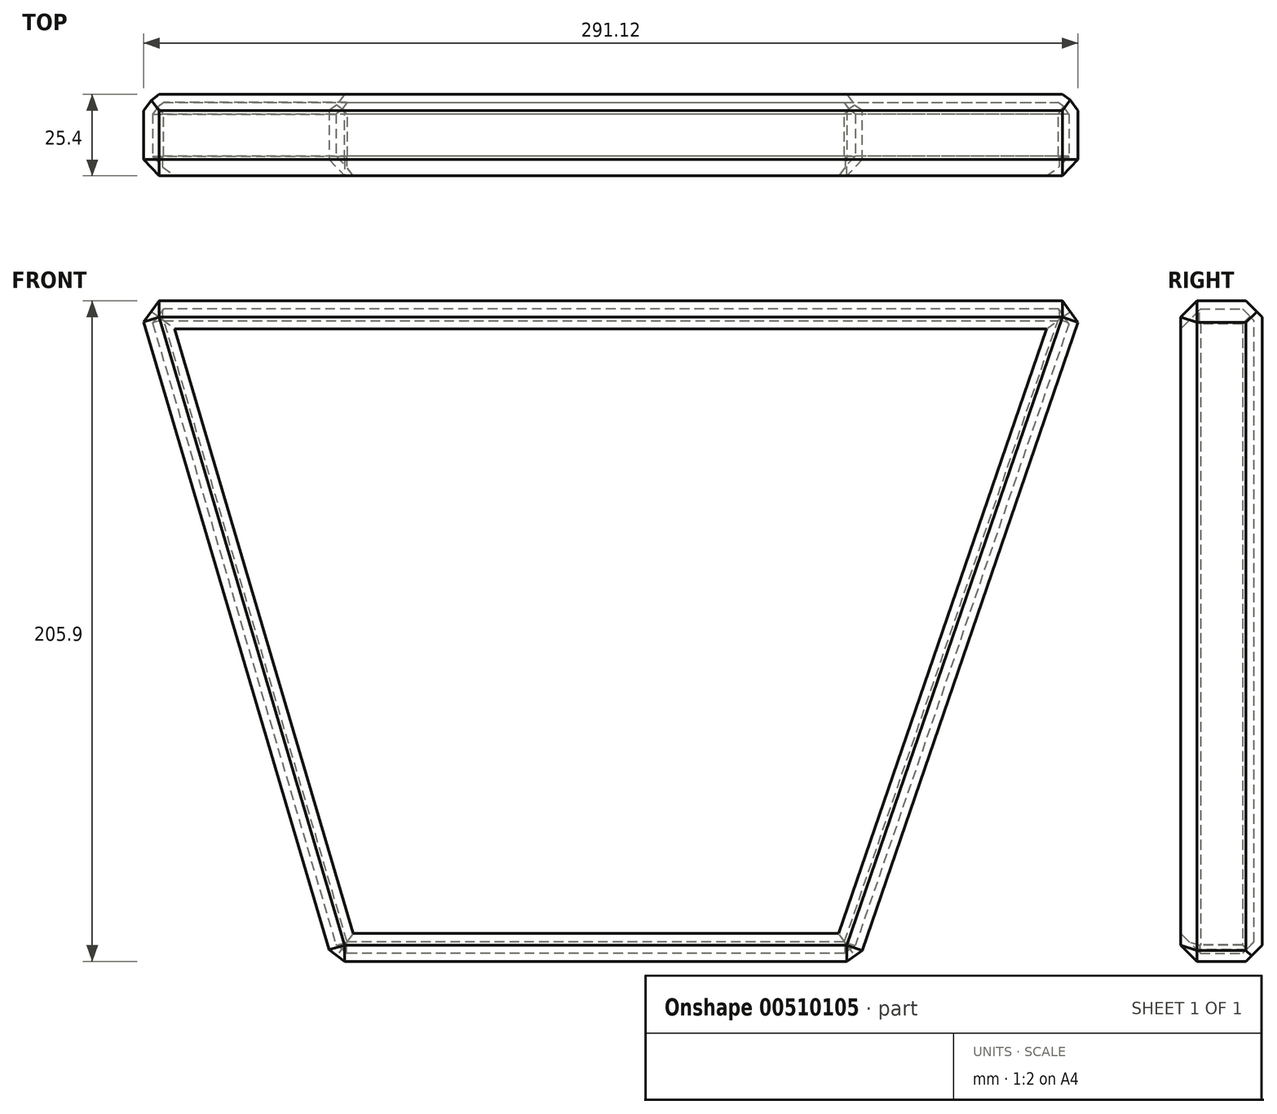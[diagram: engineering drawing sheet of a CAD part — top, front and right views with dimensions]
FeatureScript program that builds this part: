
annotation { "Feature Type Name" : "Feature", "Feature Type Description" : "" }
export const myFeature = defineFeature(function(context is Context, id is Id, definition is map)
    precondition{}
    {
        {
            var Q0;
            Q0=qCreatedBy(makeId("Front.planeOp"),FACE);
            var sketch = newSketch(context, id + "F0", { "sketchPlane" : qUnion([Q0])});
            skLineSegment(sketch, "E0.bottom", {"start": v(-83.09, -100.97) * mm, "end": v(80.84, -100.97) * mm});
            skLineSegment(sketch, "E0.top", {"start": v(-83.09, 104.93) * mm, "end": v(80.84, 104.93) * mm});
            skLineSegment(sketch, "E0.left", {"start": v(-83.09, -100.97) * mm, "end": v(-83.09, 104.93) * mm});
            skLineSegment(sketch, "E0.right", {"start": v(80.84, -100.97) * mm, "end": v(80.84, 104.93) * mm});
            skPoint(sketch, "E0.middle", {"position": v(-1.12, 1.98) * mm});
            skLineSegment(sketch, "E1", {"start": v(-83.09, -100.97) * mm, "end": v(-143.8, 104.93) * mm});
            skLineSegment(sketch, "E2", {"start": v(-143.8, 104.93) * mm, "end": v(-83.09, 104.93) * mm});
            skLineSegment(sketch, "E3", {"start": v(80.84, -100.97) * mm, "end": v(151.55, 104.93) * mm});
            skLineSegment(sketch, "E4", {"start": v(151.55, 104.93) * mm, "end": v(80.84, 104.93) * mm});
            skSolve(sketch);
        }
        {
            var Q0;
            Q0=makeQuery(id+"F0.imprint","IMPRINT",FACE,{"disambiguationData":[TD([[makeQuery(id+"F0.imprint","IMPRINT",EDGE,{"derivedFrom":sQuery(id+"F0.wireOp",EDGE,"E0.left")}),1.0]])]});
            var Q1;
            Q1=makeQuery(id+"F0.imprint","IMPRINT",FACE,{"disambiguationData":[TD([[makeQuery(id+"F0.imprint","IMPRINT",EDGE,{"derivedFrom":sQuery(id+"F0.wireOp",EDGE,"E0.right")}),-1.0]])]});
            var Q2;
            Q2=makeQuery(id+"F0.imprint","IMPRINT",FACE,{"disambiguationData":[TD([[makeQuery(id+"F0.imprint","IMPRINT",EDGE,{"derivedFrom":sQuery(id+"F0.wireOp",EDGE,"E0.bottom")}),1.0]])]});
            extrude(context, id + "F1", {"entities" : qUnion([Q0, Q1, Q2]), "depth" : 25.4 * mm});
        }
        {
            var Q0;
            Q0=makeQuery(id+"F1.opExtrude","CAP_FACE",FACE,{"disambiguationData":[OSD([sQuery(id+"F0.wireOp",EDGE,"E0.bottom"),sQuery(id+"F0.wireOp",EDGE,"E0.top"),sQuery(id+"F0.wireOp",EDGE,"E1"),sQuery(id+"F0.wireOp",EDGE,"E2"),sQuery(id+"F0.wireOp",EDGE,"E3"),sQuery(id+"F0.wireOp",EDGE,"E4")])],"isStart":true});
            chamfer(context, id + "F2", {"entities" : qUnion([Q0]), "width" : 5.08 * mm, "tangentPropagation" : true});
        }
        {
            var Q0;
            Q0=makeQuery(id+"F1.opExtrude","CAP_EDGE",EDGE,{"disambiguationData":[OSD([sQuery(id+"F0.wireOp",EDGE,"E0.bottom")])],"isStart":false});
            var Q1;
            Q1=makeQuery(id+"F1.opExtrude","CAP_EDGE",EDGE,{"disambiguationData":[OSD([sQuery(id+"F0.wireOp",EDGE,"E1")])],"isStart":false});
            var Q2;
            Q2=makeQuery(id+"F1.opExtrude","CAP_EDGE",EDGE,{"disambiguationData":[OSD([sQuery(id+"F0.wireOp",EDGE,"E3")])],"isStart":false});
            var Q3;
            Q3=makeQuery(id+"F1.opExtrude","SWEPT_EDGE",EDGE,{"disambiguationData":[OSD([sQuery(id+"F0.wireOp",EDGE,"E0.bottom"),sQuery(id+"F0.wireOp",EDGE,"E0.left"),sQuery(id+"F0.wireOp",EDGE,"E1")])]});
            var Q4;
            Q4=makeQuery(id+"F1.opExtrude","CAP_EDGE",EDGE,{"disambiguationData":[OSD([sQuery(id+"F0.wireOp",EDGE,"E0.top"),sQuery(id+"F0.wireOp",EDGE,"E2"),sQuery(id+"F0.wireOp",EDGE,"E4")])],"isStart":false});
            var Q5;
            Q5=makeQuery(id+"F1.opExtrude","SWEPT_EDGE",EDGE,{"disambiguationData":[OSD([sQuery(id+"F0.wireOp",EDGE,"E3"),sQuery(id+"F0.wireOp",EDGE,"E4")])]});
            var Q6;
            Q6=makeQuery(id+"F1.opExtrude","SWEPT_EDGE",EDGE,{"disambiguationData":[OSD([sQuery(id+"F0.wireOp",EDGE,"E0.bottom"),sQuery(id+"F0.wireOp",EDGE,"E0.right"),sQuery(id+"F0.wireOp",EDGE,"E3")])]});
            var Q7;
            Q7=makeQuery(id+"F1.opExtrude","SWEPT_EDGE",EDGE,{"disambiguationData":[OSD([sQuery(id+"F0.wireOp",EDGE,"E1"),sQuery(id+"F0.wireOp",EDGE,"E2")])]});
            chamfer(context, id + "F3", {"entities" : qUnion([Q0, Q1, Q2, Q3, Q4, Q5, Q6, Q7]), "width" : 5.08 * mm, "tangentPropagation" : true});
        }
        {
            var Q0;
            Q0=makeQuery(id+"F1.opExtrude","CAP_FACE",FACE,{"disambiguationData":[OSD([sQuery(id+"F0.wireOp",EDGE,"E0.bottom"),sQuery(id+"F0.wireOp",EDGE,"E0.top"),sQuery(id+"F0.wireOp",EDGE,"E1"),sQuery(id+"F0.wireOp",EDGE,"E2"),sQuery(id+"F0.wireOp",EDGE,"E3"),sQuery(id+"F0.wireOp",EDGE,"E4")])],"isStart":false});
            shell(context, id + "F4", {"entities" : qUnion([Q0]), "thickness" : 2.54 * mm});
        }
    });
